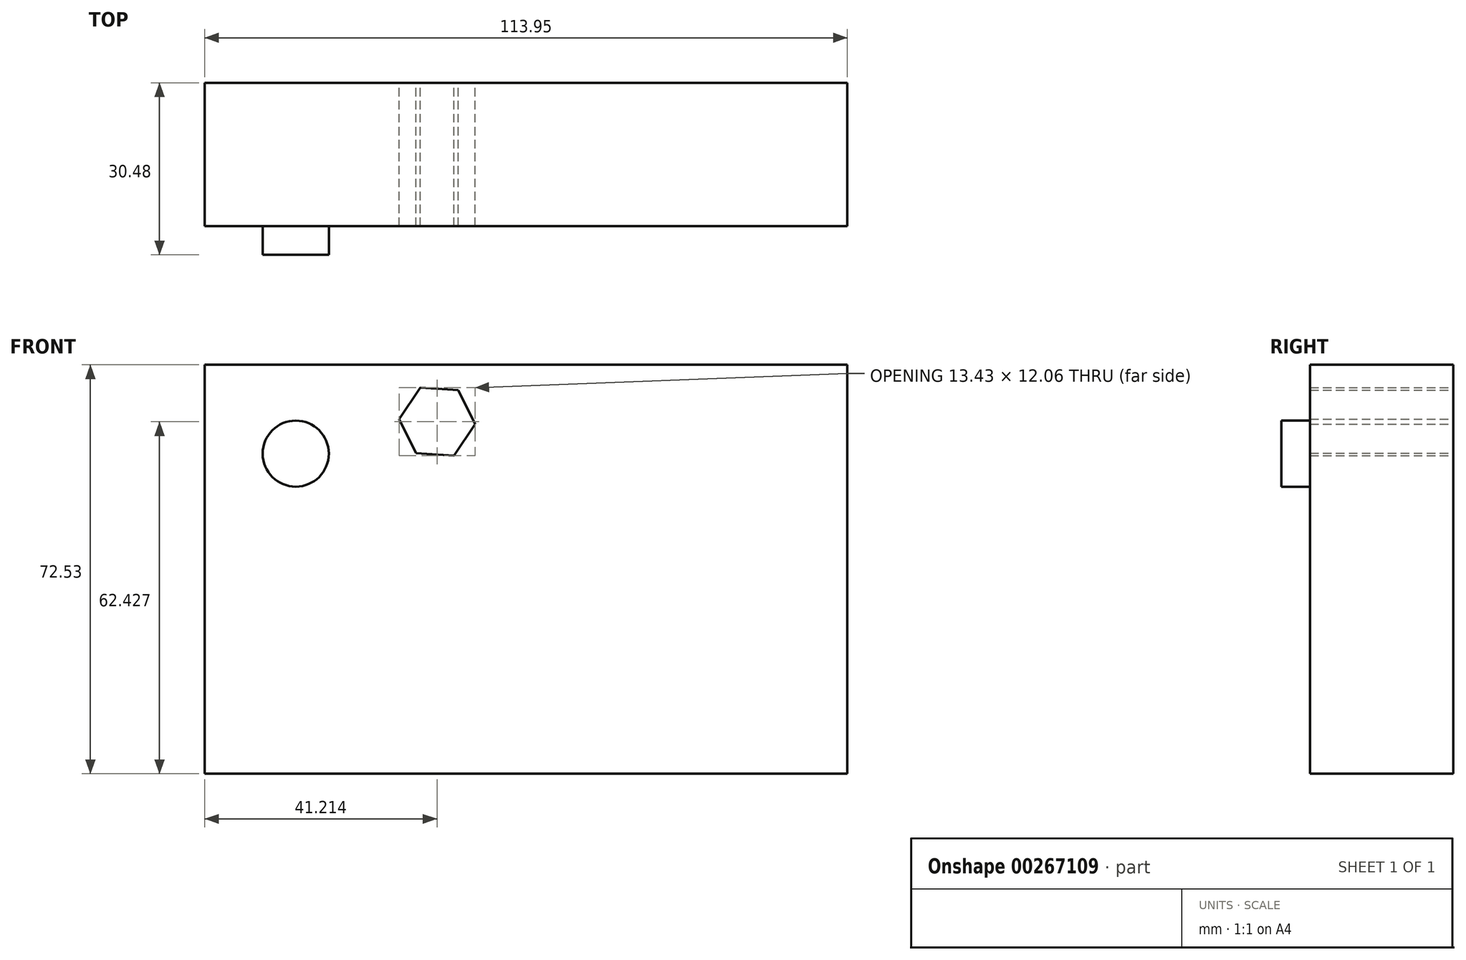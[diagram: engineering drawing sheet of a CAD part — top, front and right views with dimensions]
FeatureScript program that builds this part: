
annotation { "Feature Type Name" : "Feature", "Feature Type Description" : "" }
export const myFeature = defineFeature(function(context is Context, id is Id, definition is map)
    precondition{}
    {
        {
            var Q0;
            Q0=qCreatedBy(makeId("Front.planeOp"),FACE);
            var sketch = newSketch(context, id + "F0", { "sketchPlane" : qUnion([Q0])});
            skLineSegment(sketch, "E0.bottom", {"start": v(-49.7, 33.54) * mm, "end": v(64.25, 33.54) * mm});
            skLineSegment(sketch, "E0.top", {"start": v(-49.7, -39) * mm, "end": v(64.25, -39) * mm});
            skLineSegment(sketch, "E0.left", {"start": v(-49.7, 33.54) * mm, "end": v(-49.7, -39) * mm});
            skLineSegment(sketch, "E0.right", {"start": v(64.25, 33.54) * mm, "end": v(64.25, -39) * mm});
            skCircle(sketch, "E1", {"center": v(-33.54, 17.78) * mm, "radius": 5.86 * mm});
            skCircle(sketch, "E2.cCircle", {"center": v(-8.49, 23.44) * mm, "radius": 5.83 * mm, "construction": true});
            skLineSegment(sketch, "E2.0", {"start": v(-1.77, 23) * mm, "end": v(-5.5, 17.4) * mm});
            skLineSegment(sketch, "E2.1", {"start": v(-5.5, 17.4) * mm, "end": v(-12.22, 17.84) * mm});
            skLineSegment(sketch, "E2.2", {"start": v(-12.22, 17.84) * mm, "end": v(-15.2, 23.87) * mm});
            skLineSegment(sketch, "E2.3", {"start": v(-15.2, 23.87) * mm, "end": v(-11.47, 29.47) * mm});
            skLineSegment(sketch, "E2.4", {"start": v(-11.47, 29.47) * mm, "end": v(-4.75, 29.04) * mm});
            skLineSegment(sketch, "E2.5", {"start": v(-4.75, 29.04) * mm, "end": v(-1.77, 23) * mm});
            skPoint(sketch, "E2.0.midPoint", {"position": v(-3.64, 20.2) * mm});
            skSolve(sketch);
        }
        {
            var Q0;
            Q0=makeQuery(id+"F0.imprint","IMPRINT",FACE,{"disambiguationData":[TD([[makeQuery(id+"F0.imprint","IMPRINT",EDGE,{"derivedFrom":sQuery(id+"F0.wireOp",EDGE,"E0.bottom")}),-1.0]])]});
            extrude(context, id + "F1", {"entities" : qUnion([Q0]), "depth" : 25.4 * mm});
        }
        {
            var Q0;
            Q0=makeQuery(id+"F0.imprint","IMPRINT",FACE,{"disambiguationData":[TD([[makeQuery(id+"F0.imprint","IMPRINT",EDGE,{"derivedFrom":sQuery(id+"F0.wireOp",EDGE,"E1")}),1.0]])]});
            extrude(context, id + "F2", {"entities" : qUnion([Q0]), "operationType" : NewBodyOperationType.ADD, "depth" : 30.48 * mm});
        }
    });
